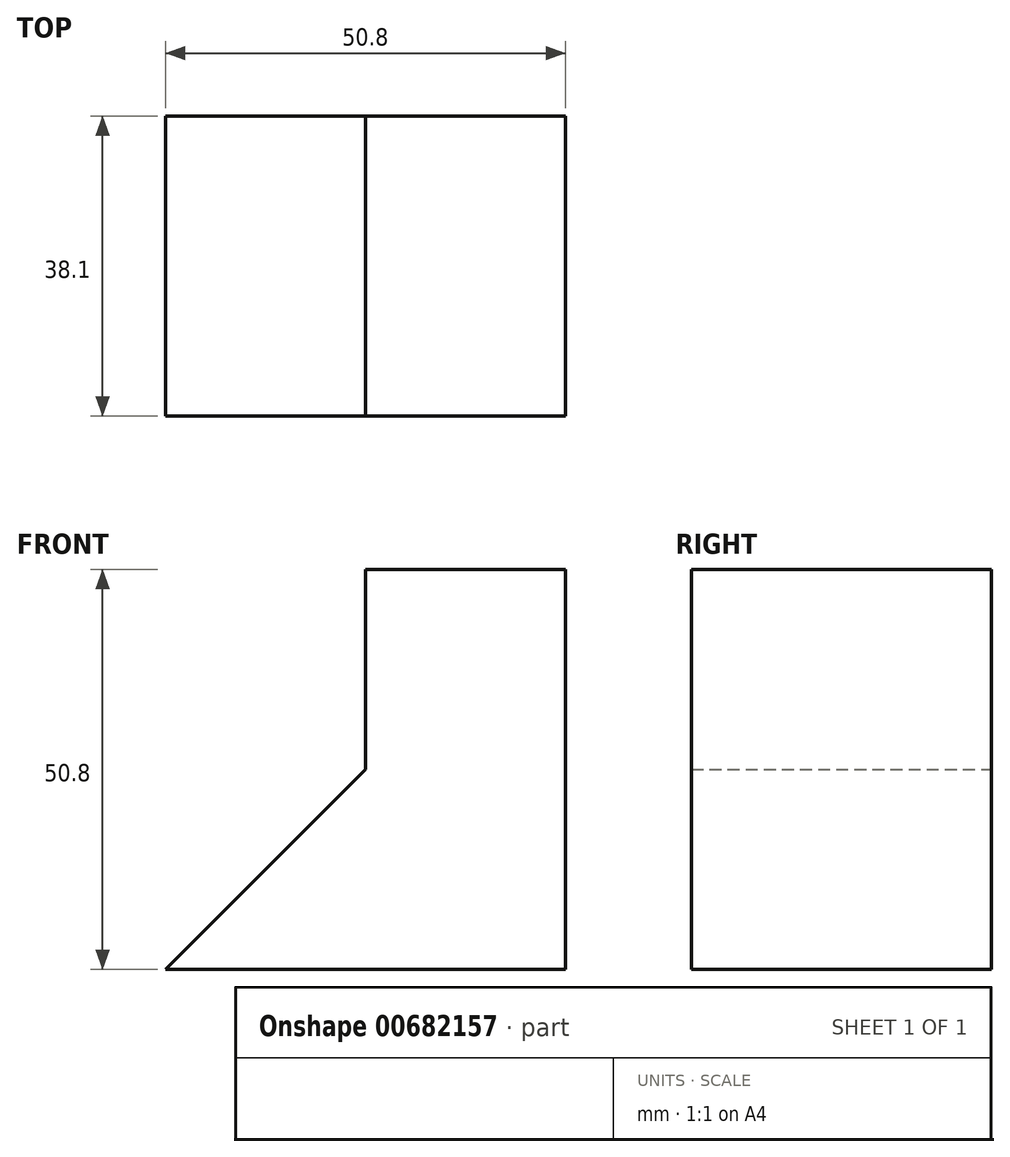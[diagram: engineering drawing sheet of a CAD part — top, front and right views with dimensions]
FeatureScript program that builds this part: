
annotation { "Feature Type Name" : "Feature", "Feature Type Description" : "" }
export const myFeature = defineFeature(function(context is Context, id is Id, definition is map)
    precondition{}
    {
        {
            var Q0;
            Q0=qCreatedBy(makeId("Front.planeOp"),FACE);
            var sketch = newSketch(context, id + "F0", { "sketchPlane" : qUnion([Q0])});
            skLineSegment(sketch, "E0", {"start": v(-38.2, -27.04) * mm, "end": v(12.6, -27.04) * mm});
            skLineSegment(sketch, "E1", {"start": v(12.6, -27.04) * mm, "end": v(12.6, 23.76) * mm});
            skLineSegment(sketch, "E2", {"start": v(12.6, 23.76) * mm, "end": v(-12.8, 23.76) * mm});
            skLineSegment(sketch, "E3", {"start": v(-12.8, 23.76) * mm, "end": v(-12.8, -1.64) * mm});
            skLineSegment(sketch, "E4", {"start": v(-12.8, -1.64) * mm, "end": v(-38.2, -27.04) * mm});
            skSolve(sketch);
        }
        {
            var Q0;
            Q0=makeQuery(id+"F0.imprint","IMPRINT",FACE,{"disambiguationData":[TD([[makeQuery(id+"F0.imprint","IMPRINT",EDGE,{"derivedFrom":sQuery(id+"F0.wireOp",EDGE,"E0")}),1.0]])]});
            extrude(context, id + "F1", {"entities" : qUnion([Q0]), "depth" : 38.1 * mm, "offsetDistance" : 25.4 * mm});
        }
    });
